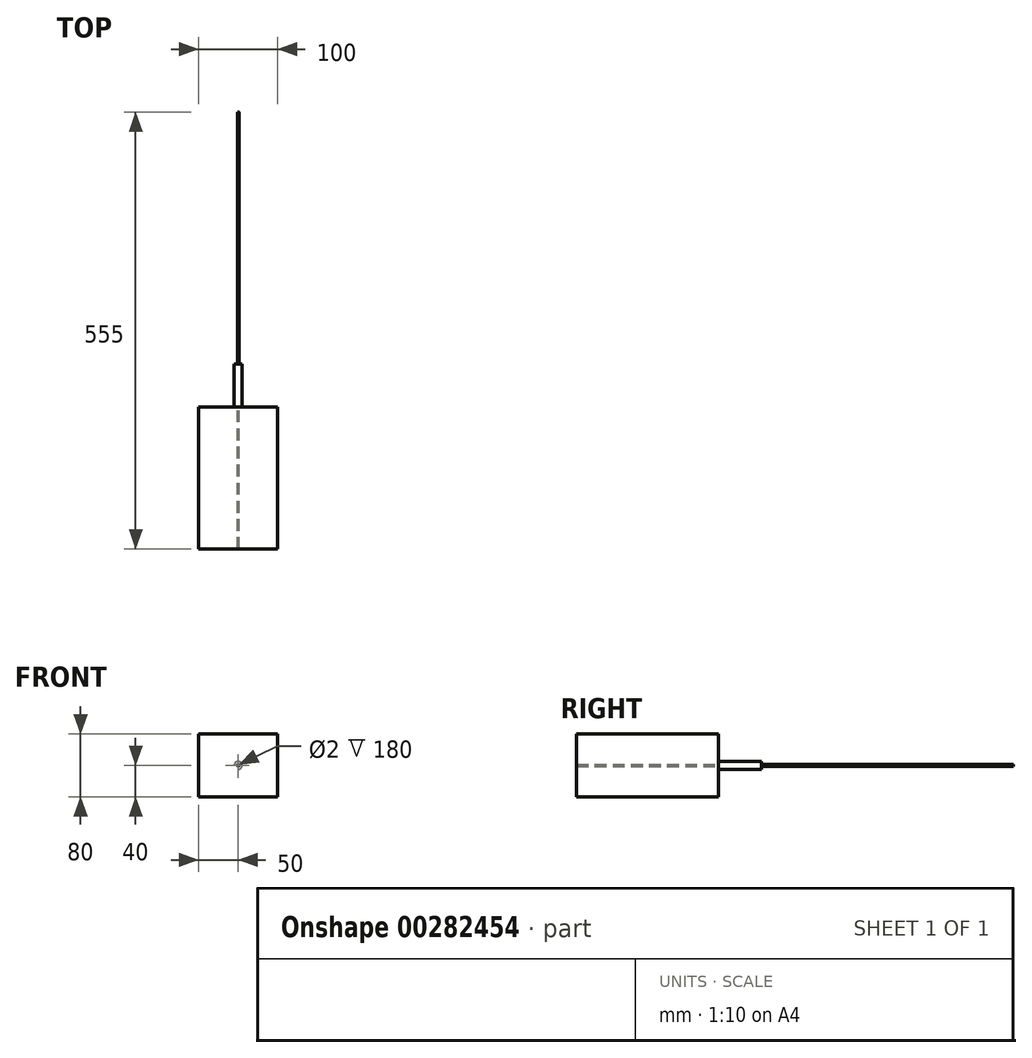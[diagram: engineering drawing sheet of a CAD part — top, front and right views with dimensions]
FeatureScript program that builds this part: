
annotation { "Feature Type Name" : "Feature", "Feature Type Description" : "" }
export const myFeature = defineFeature(function(context is Context, id is Id, definition is map)
    precondition{}
    {
        {
            var Q0;
            Q0=qCreatedBy(makeId("Front.planeOp"),FACE);
            var sketch = newSketch(context, id + "F0", { "sketchPlane" : qUnion([Q0])});
            skLineSegment(sketch, "E0.bottom", {"start": v(-50, 40) * mm, "end": v(50, 40) * mm});
            skLineSegment(sketch, "E0.top", {"start": v(-50, -40) * mm, "end": v(50, -40) * mm});
            skLineSegment(sketch, "E0.left", {"start": v(-50, 40) * mm, "end": v(-50, -40) * mm});
            skLineSegment(sketch, "E0.right", {"start": v(50, 40) * mm, "end": v(50, -40) * mm});
            skPoint(sketch, "E0.middle", {"position": v(0, 0) * mm});
            skCircle(sketch, "E1", {"center": v(0, 0) * mm, "radius": 1 * mm});
            skSolve(sketch);
        }
        {
            var Q0;
            Q0=makeQuery(id+"F0.imprint","IMPRINT",FACE,{"disambiguationData":[TD([[makeQuery(id+"F0.imprint","IMPRINT",EDGE,{"derivedFrom":sQuery(id+"F0.wireOp",EDGE,"E0.bottom")}),-1.0]])]});
            extrude(context, id + "F1", {"entities" : qUnion([Q0]), "depth" : 180 * mm});
        }
        {
            var Q0;
            Q0=makeQuery(id+"F1.opExtrude","CAP_FACE",FACE,{"disambiguationData":[OSD([sQuery(id+"F0.wireOp",EDGE,"E0.bottom"),sQuery(id+"F0.wireOp",EDGE,"E0.top"),sQuery(id+"F0.wireOp",EDGE,"E0.left"),sQuery(id+"F0.wireOp",EDGE,"E0.right"),sQuery(id+"F0.wireOp",EDGE,"E1")])],"isStart":true});
            var sketch = newSketch(context, id + "F2", { "sketchPlane" : qUnion([Q0])});
            skCircle(sketch, "E2", {"center": v(0, 0) * mm, "radius": 5 * mm});
            skSolve(sketch);
        }
        {
            var Q0;
            Q0=makeQuery(id+"F2.imprint","IMPRINT",FACE,{"disambiguationData":[TD([[makeQuery(id+"F2.imprint","IMPRINT",EDGE,{"derivedFrom":makeQuery(id+"F1.opExtrude","CAP_EDGE",EDGE,{"disambiguationData":[OSD([sQuery(id+"F0.wireOp",EDGE,"E1")])],"isStart":true})}),-1.0]])]});
            extrude(context, id + "F3", {"entities" : qUnion([Q0]), "operationType" : NewBodyOperationType.ADD, "depth" : 375 * mm});
        }
        {
            var Q0;
            Q0 = qSketchRegion(id + "F2", true);
            extrude(context, id + "F4", {"entities" : qUnion([Q0]), "operationType" : NewBodyOperationType.ADD, "depth" : 55 * mm});
        }
    });
